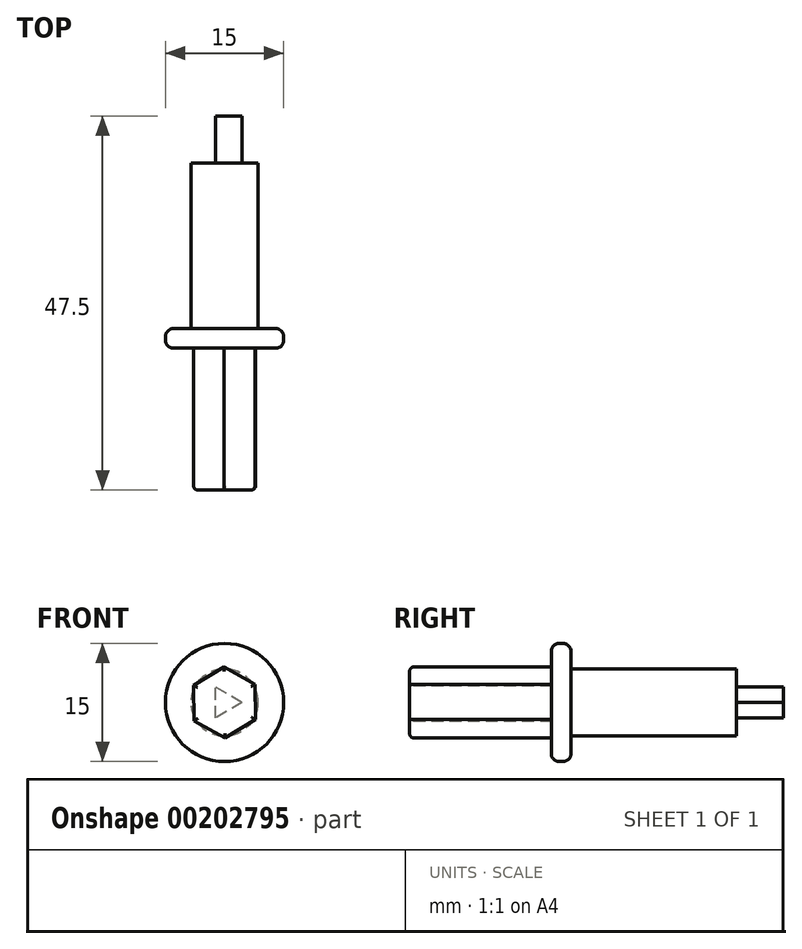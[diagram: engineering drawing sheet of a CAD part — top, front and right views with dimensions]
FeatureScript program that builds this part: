
annotation { "Feature Type Name" : "Feature", "Feature Type Description" : "" }
export const myFeature = defineFeature(function(context is Context, id is Id, definition is map)
    precondition{}
    {
        {
            var Q0;
            Q0=qCreatedBy(makeId("Front.planeOp"),FACE);
            var sketch = newSketch(context, id + "F0", { "sketchPlane" : qUnion([Q0])});
            skCircle(sketch, "E0", {"center": v(0, 0) * mm, "radius": 4.25 * mm});
            skCircle(sketch, "E1.0", {"center": v(0, 0) * mm, "radius": 2.25 * mm, "construction": true});
            skLineSegment(sketch, "E2.0", {"start": v(2.25, 0) * mm, "end": v(-1.13, -1.95) * mm});
            skLineSegment(sketch, "E2.1", {"start": v(-1.13, -1.95) * mm, "end": v(-1.12, 1.95) * mm});
            skLineSegment(sketch, "E2.2", {"start": v(-1.12, 1.95) * mm, "end": v(2.25, 0) * mm});
            skSolve(sketch);
        }
        {
            var Q0;
            Q0=makeQuery(id+"F0.imprint","IMPRINT",FACE,{"disambiguationData":[TD([[makeQuery(id+"F0.imprint","IMPRINT",EDGE,{"derivedFrom":sQuery(id+"F0.wireOp",EDGE,"E0")}),1.0]])]});
            var Q1;
            Q1=makeQuery(id+"F0.imprint","IMPRINT",FACE,{"disambiguationData":[TD([[makeQuery(id+"F0.imprint","IMPRINT",EDGE,{"derivedFrom":sQuery(id+"F0.wireOp",EDGE,"E2.0")}),-1.0]])]});
            extrude(context, id + "F1", {"entities" : qUnion([Q0, Q1]), "depth" : 21 * mm});
        }
        {
            var Q0;
            Q0=makeQuery(id+"F0.imprint","IMPRINT",FACE,{"disambiguationData":[TD([[makeQuery(id+"F0.imprint","IMPRINT",EDGE,{"derivedFrom":sQuery(id+"F0.wireOp",EDGE,"E2.0")}),-1.0]])]});
            extrude(context, id + "F2", {"entities" : qUnion([Q0]), "operationType" : NewBodyOperationType.ADD, "oppositeDirection" : true, "depth" : 6 * mm});
        }
        {
            var Q0;
            Q0=makeQuery(id+"F1.opExtrude","CAP_FACE",FACE,{"disambiguationData":[OSD([sQuery(id+"F0.wireOp",EDGE,"E0")])],"isStart":false});
            var sketch = newSketch(context, id + "F3", { "sketchPlane" : qUnion([Q0])});
            skCircle(sketch, "E3", {"center": v(0, 0) * mm, "radius": 7.5 * mm});
            skSolve(sketch);
        }
        {
            var Q0;
            Q0=makeQuery(id+"F3.imprint","IMPRINT",FACE,{"disambiguationData":[TD([[makeQuery(id+"F3.imprint","IMPRINT",EDGE,{"derivedFrom":sQuery(id+"F3.wireOp",EDGE,"E3")}),1.0]])]});
            var Q1;
            Q1=makeQuery(id+"F3.imprint","IMPRINT",FACE,{"disambiguationData":[TD([[makeQuery(id+"F3.imprint","IMPRINT",EDGE,{"derivedFrom":makeQuery(id+"F1.opExtrude","CAP_EDGE",EDGE,{"disambiguationData":[OSD([sQuery(id+"F0.wireOp",EDGE,"E0")])],"isStart":false})}),1.0]])]});
            extrude(context, id + "F4", {"entities" : qUnion([Q0, Q1]), "operationType" : NewBodyOperationType.ADD, "depth" : 2.5 * mm});
        }
        {
            var Q0;
            Q0=makeQuery(id+"F4.opExtrude","CAP_FACE",FACE,{"disambiguationData":[OSD([sQuery(id+"F3.wireOp",EDGE,"E3")])],"isStart":false});
            var sketch = newSketch(context, id + "F5", { "sketchPlane" : qUnion([Q0])});
            skCircle(sketch, "E4", {"center": v(0, 0) * mm, "radius": 4.5 * mm, "construction": true});
            skLineSegment(sketch, "E5.0", {"start": v(3.93, -2.18) * mm, "end": v(0.08, -4.5) * mm});
            skLineSegment(sketch, "E5.1", {"start": v(0.08, -4.5) * mm, "end": v(-3.86, -2.32) * mm});
            skLineSegment(sketch, "E5.2", {"start": v(-3.86, -2.32) * mm, "end": v(-3.93, 2.18) * mm});
            skLineSegment(sketch, "E5.3", {"start": v(-3.93, 2.18) * mm, "end": v(-0.08, 4.5) * mm});
            skLineSegment(sketch, "E5.4", {"start": v(-0.08, 4.5) * mm, "end": v(3.86, 2.32) * mm});
            skLineSegment(sketch, "E5.5", {"start": v(3.86, 2.32) * mm, "end": v(3.93, -2.18) * mm});
            skSolve(sketch);
        }
        {
            var Q0;
            Q0=makeQuery(id+"F5.imprint","IMPRINT",FACE,{"disambiguationData":[TD([[makeQuery(id+"F5.imprint","IMPRINT",EDGE,{"derivedFrom":sQuery(id+"F5.wireOp",EDGE,"E5.0")}),-1.0]])]});
            extrude(context, id + "F6", {"entities" : qUnion([Q0]), "operationType" : NewBodyOperationType.ADD, "depth" : 18 * mm});
        }
        {
            var Q0;
            Q0=makeQuery(id+"F6.opExtrude","CAP_EDGE",EDGE,{"disambiguationData":[OSD([sQuery(id+"F5.wireOp",EDGE,"E5.0")])],"isStart":false});
            var Q1;
            Q1=makeQuery(id+"F6.opExtrude","CAP_EDGE",EDGE,{"disambiguationData":[OSD([sQuery(id+"F5.wireOp",EDGE,"E5.1")])],"isStart":false});
            var Q2;
            Q2=makeQuery(id+"F6.opExtrude","CAP_EDGE",EDGE,{"disambiguationData":[OSD([sQuery(id+"F5.wireOp",EDGE,"E5.2")])],"isStart":false});
            var Q3;
            Q3=makeQuery(id+"F6.opExtrude","CAP_EDGE",EDGE,{"disambiguationData":[OSD([sQuery(id+"F5.wireOp",EDGE,"E5.3")])],"isStart":false});
            var Q4;
            Q4=makeQuery(id+"F6.opExtrude","CAP_EDGE",EDGE,{"disambiguationData":[OSD([sQuery(id+"F5.wireOp",EDGE,"E5.4")])],"isStart":false});
            var Q5;
            Q5=makeQuery(id+"F6.opExtrude","CAP_EDGE",EDGE,{"disambiguationData":[OSD([sQuery(id+"F5.wireOp",EDGE,"E5.5")])],"isStart":false});
            fillet(context, id + "F7", {"entities" : qUnion([Q0, Q1, Q2, Q3, Q4, Q5]), "radius" : .5 * mm, "tangentPropagation" : true, "allowEdgeOverflow" : false});
        }
        {
            var Q0;
            Q0=makeQuery(id+"F4.opExtrude","CAP_EDGE",EDGE,{"disambiguationData":[OSD([sQuery(id+"F3.wireOp",EDGE,"E3")])],"isStart":false});
            var Q1;
            Q1=makeQuery(id+"F4.opExtrude","CAP_EDGE",EDGE,{"disambiguationData":[OSD([sQuery(id+"F3.wireOp",EDGE,"E3")])],"isStart":true});
            fillet(context, id + "F8", {"entities" : qUnion([Q0, Q1]), "radius" : 1 * mm, "tangentPropagation" : true, "allowEdgeOverflow" : false});
        }
    });
